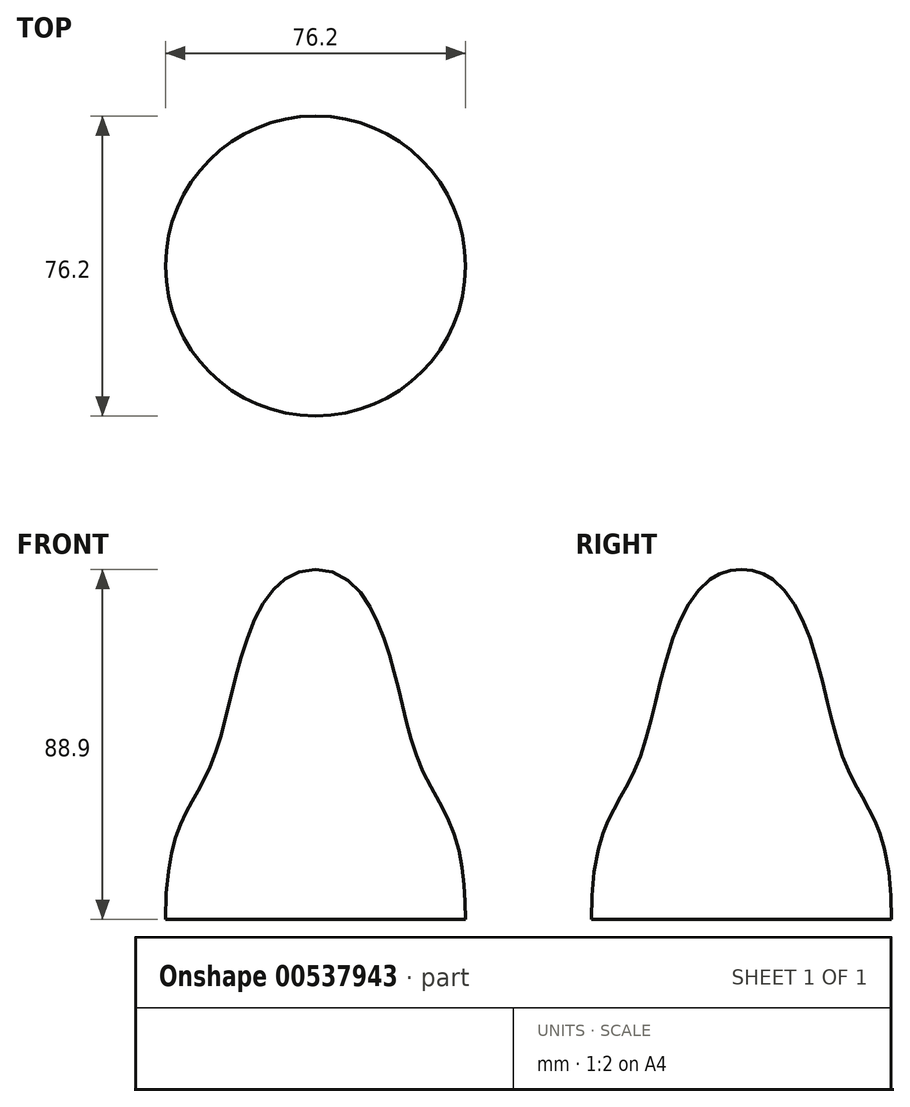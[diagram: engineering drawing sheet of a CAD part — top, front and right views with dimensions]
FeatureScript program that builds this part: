
annotation { "Feature Type Name" : "Feature", "Feature Type Description" : "" }
export const myFeature = defineFeature(function(context is Context, id is Id, definition is map)
    precondition{}
    {
        {
            var Q0;
            Q0=qCreatedBy(makeId("Front.planeOp"),FACE);
            var sketch = newSketch(context, id + "F0", { "sketchPlane" : qUnion([Q0])});
            skLineSegment(sketch, "E0", {"start": v(0, 0) * mm, "end": v(0, 88.9) * mm});
            skLineSegment(sketch, "E1", {"start": v(0, 0) * mm, "end": v(-38.1, 0) * mm});
            skFitSpline(sketch, "E2", {"points": [v(-38.1, 0) * mm, v(-25.4, 42.26) * mm, v(0, 88.9) * mm], "startDerivative": vector(0, 166.06) * mm, "endDerivative": vector(102.56, 0) * mm});
            skSolve(sketch);
        }
        {
            var Q0;
            Q0=makeQuery(id+"F0.imprint","IMPRINT",FACE,{"disambiguationData":[TD([[makeQuery(id+"F0.imprint","IMPRINT",EDGE,{"derivedFrom":sQuery(id+"F0.wireOp",EDGE,"E0")}),1.0]])]});
            var Q1;
            Q1=sQuery(id+"F0.wireOp",EDGE,"E0");
            revolve(context, id + "F1", {"entities" : qUnion([Q0]), "axis" : qUnion([Q1]), "revolveType" : RevolveType.FULL});
        }
    });
